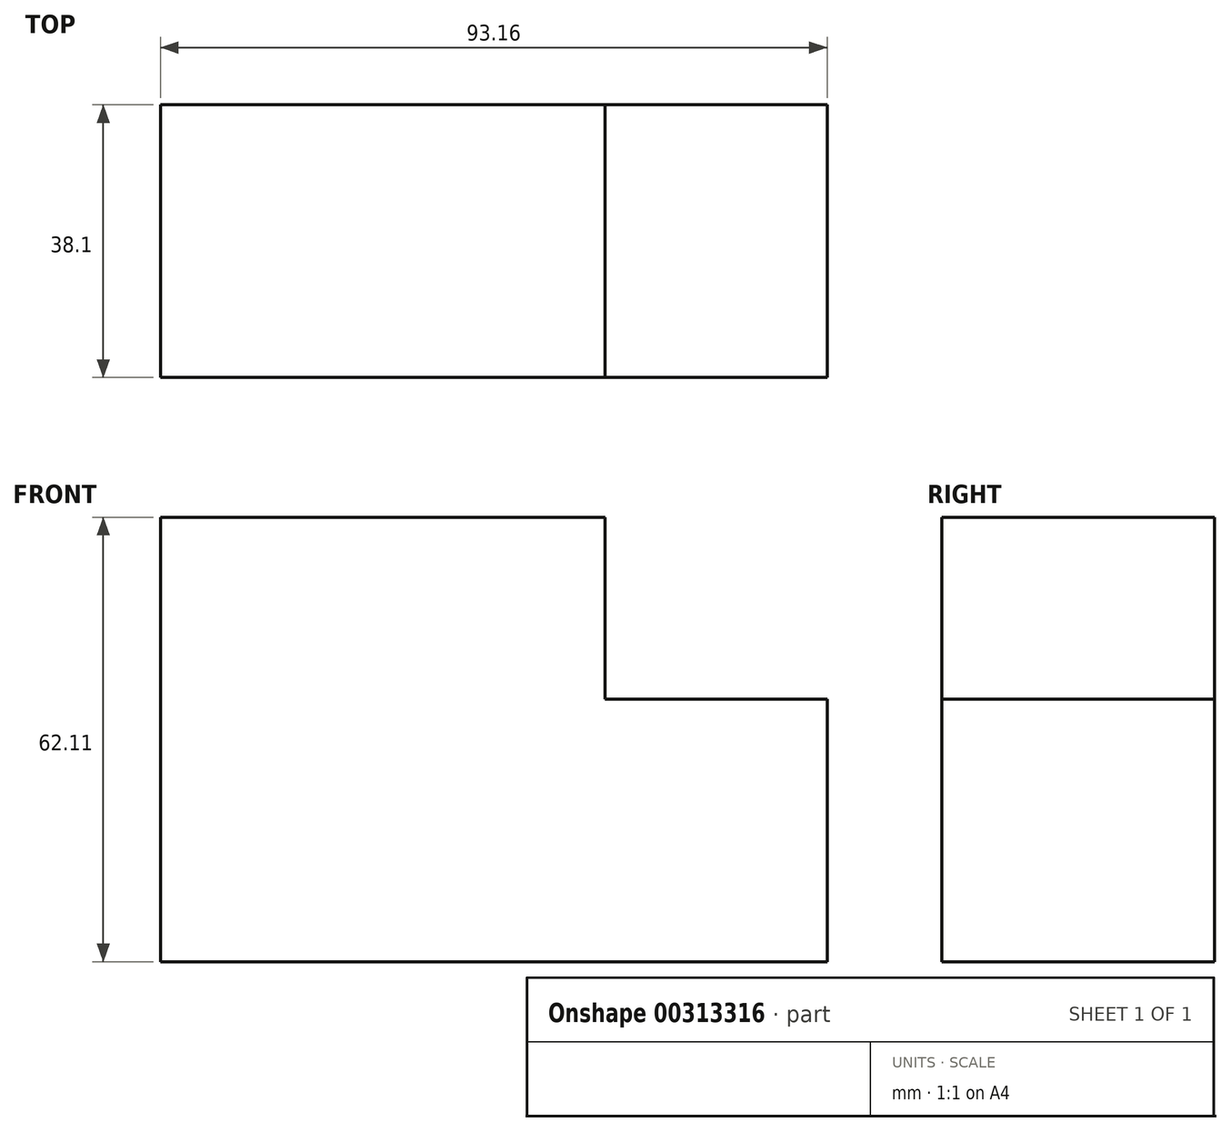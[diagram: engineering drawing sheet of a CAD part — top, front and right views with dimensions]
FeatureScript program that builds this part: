
annotation { "Feature Type Name" : "Feature", "Feature Type Description" : "" }
export const myFeature = defineFeature(function(context is Context, id is Id, definition is map)
    precondition{}
    {
        {
            var Q0;
            Q0=qCreatedBy(makeId("Front.planeOp"),FACE);
            var sketch = newSketch(context, id + "F0", { "sketchPlane" : qUnion([Q0])});
            skLineSegment(sketch, "E0", {"start": v(-49.83, -25.93) * mm, "end": v(43.33, -25.93) * mm});
            skLineSegment(sketch, "E1", {"start": v(-49.83, -25.93) * mm, "end": v(-49.83, 36.18) * mm});
            skLineSegment(sketch, "E2", {"start": v(-49.83, 36.18) * mm, "end": v(12.28, 36.18) * mm});
            skLineSegment(sketch, "E3", {"start": v(12.28, 36.18) * mm, "end": v(12.28, 10.78) * mm});
            skLineSegment(sketch, "E4", {"start": v(12.28, 10.78) * mm, "end": v(37.68, 10.78) * mm});
            skLineSegment(sketch, "E5", {"start": v(43.33, -25.93) * mm, "end": v(43.33, 10.78) * mm});
            skLineSegment(sketch, "E6", {"start": v(37.68, 10.78) * mm, "end": v(43.33, 10.78) * mm});
            skSolve(sketch);
        }
        {
            var Q0;
            Q0=makeQuery(id+"F0.imprint","IMPRINT",FACE,{"disambiguationData":[TD([[makeQuery(id+"F0.imprint","IMPRINT",EDGE,{"derivedFrom":sQuery(id+"F0.wireOp",EDGE,"E0")}),1.0]])]});
            extrude(context, id + "F1", {"entities" : qUnion([Q0]), "depth" : 38.1 * mm});
        }
    });
